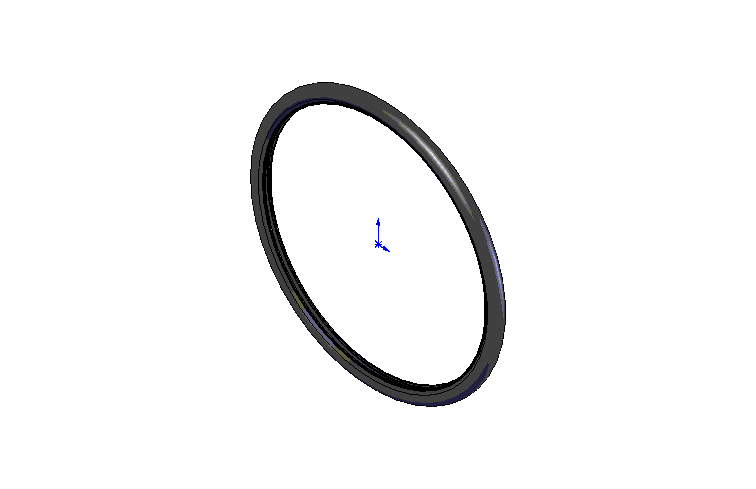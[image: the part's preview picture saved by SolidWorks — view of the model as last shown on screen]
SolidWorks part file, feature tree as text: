
SOLIDWORKS PART (.sldprt)
format: sldprt  version: not decoded by parser v0  size: 415,744 bytes
history: native  units: mm
features: plane x3, fillet x3, material x1, sketch x1, revolve x1, shell x1 (+10 scaffold rows collapsed)
feature tree (20):
  scaffold x10  (default folders/planes/origin — collapsed)
  material  "Matériau <non spécifié>"
  plane  "Plan de face"
  plane  "Plan de dessus"
  plane  "Plan de droite"
  sketch  "Esquisse1"  dims[c1.D1=36.0mm c1.D2=30.0mm c1.D6=1.5mm c1.D9=0.5mm c1.D3=705.0mm c2.D2=18.0mm c2.D4=5.5mm c2.D5=624.0mm c3.D2=18.0mm c3.D4=19.0mm c3.D7=3.0mm c3.D8=4.0mm c4.D7=2.5mm]
  revolve  "Révolution1"  Angle=360deg
  fillet  "Congé1"  Radius=0.5mm
  fillet  "Congé2"  Radius=0.4mm
  shell  "Coque1"  Thickness=3mm
  fillet  "Congé3"  Radius=0.5mm
decode coverage: 6 of 6 modeling features carry decoded parameters
note: suppression state not decoded; provenance and decode notes live in map.json
